# Revit family: 3466A_NX_Network_Interface_Module
name_source: partatom
category: Communication Devices
units: mm (PartAtom-declared; Revit-internal decimal feet)

## family parameters
Cut with Voids When Loaded = No
Host = Face
Maintain Annotation Orientation = No
OmniClass Number = 23.85.80.11.27
OmniClass Title = Lighting Controls
Part Type = Normal
Room Calculation Point = No
Round Connector Dimension = Use Diameter
Shared = Yes

## types (1)
- 3466A_NX_Network_Interface_Module
    Apparent Load = 0 VA
    Assembly Code = D5090
    Black Material = Paint -  Black Matte Textured
    Default Elevation = 48 "
    Description = It provides a simple way to incorporate standard dry contact inputs and outputs into the NX control
    Features = Allows connection of multiple accessory modules in series
• Discovered as a control device and with visibility in the Area
Controller GUI
• Repeats communication signal to extend network length
• Integral link indicators confirm network segment status
• Ribbon cable connection to accessory modules provided
• Power LED indicator confirms presence of accessory DC power
• DIN rail mounting in the NX Accessory Enclosure
    Green Element = Plastic -  Green
    Input Power = 24VDC, 800mA max current via network cable
    Manufacturer = NX Lighting Controls
    Model = NX Dry Contact Module
    Output Power = 24VDC power supplied to connected accessory modules
    Steel = Metal-Galvanized_Steel
    Type Comments = NX Network Interface Module
    URL = https://www.currentlighting.com
    Voltage = 24 V
    Warranty = 5-Years Warranty
    White Element = Metal-Galvanized_Steel

## geometry (parser evidence)
native form markers: Sweep x2
no freeform markers — native parametric forms only
